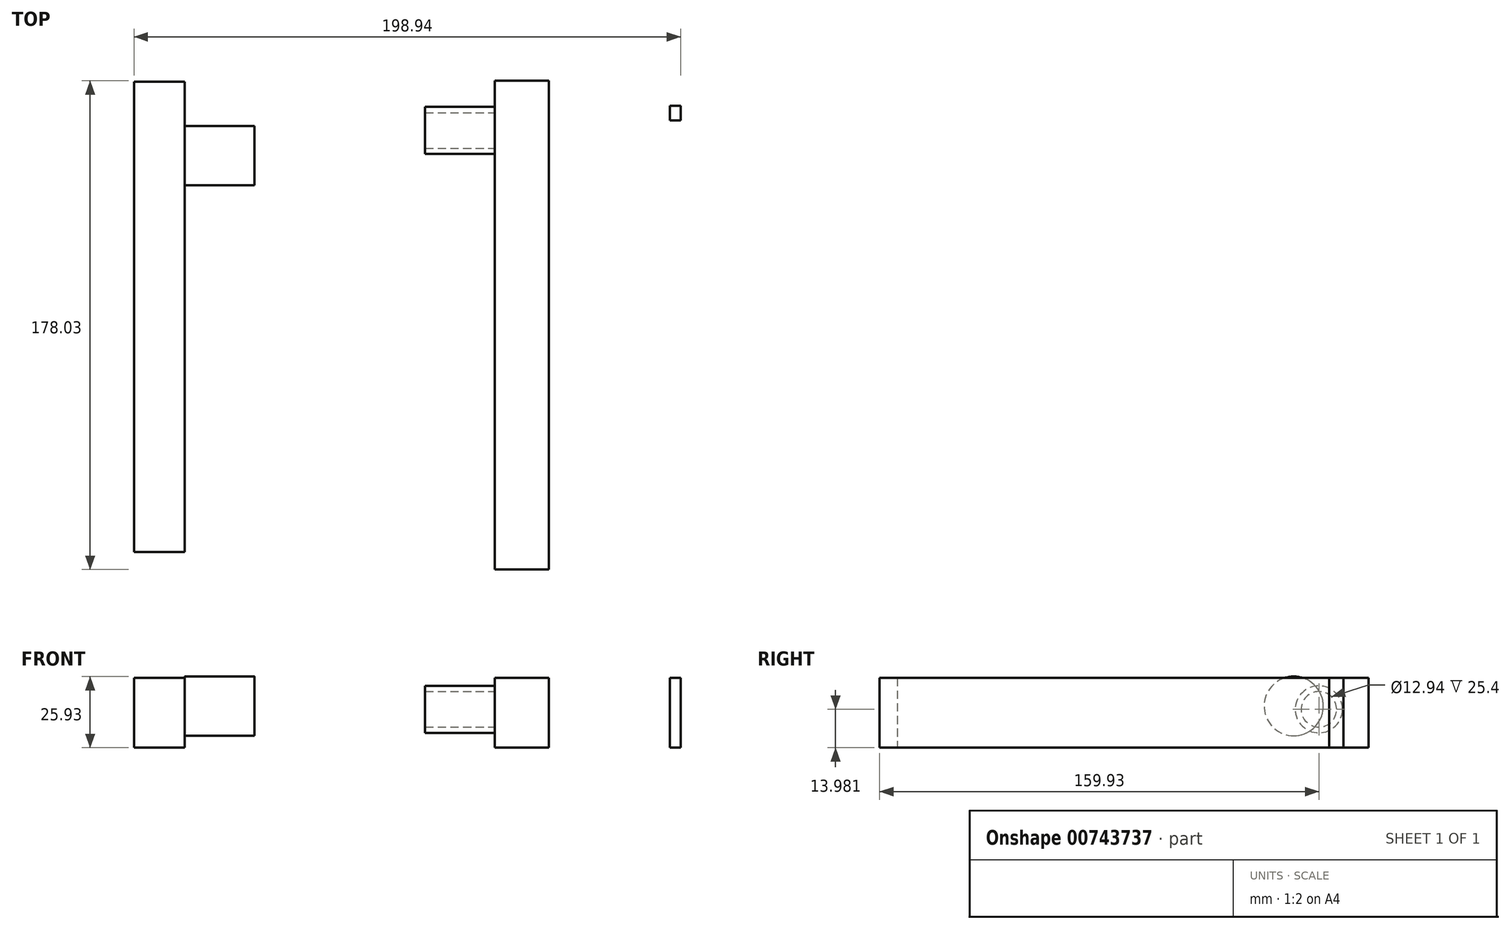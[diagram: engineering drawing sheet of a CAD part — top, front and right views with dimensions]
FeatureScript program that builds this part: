
annotation { "Feature Type Name" : "Feature", "Feature Type Description" : "" }
export const myFeature = defineFeature(function(context is Context, id is Id, definition is map)
    precondition{}
    {
        {
            var Q0;
            Q0=qCreatedBy(makeId("Top.planeOp"),FACE);
            var sketch = newSketch(context, id + "F0", { "sketchPlane" : qUnion([Q0])});
            skLineSegment(sketch, "E0.bottom", {"start": v(119.59, 61.49) * mm, "end": v(123.48, 61.49) * mm});
            skLineSegment(sketch, "E0.top", {"start": v(119.59, 66.74) * mm, "end": v(123.48, 66.74) * mm});
            skLineSegment(sketch, "E0.left", {"start": v(119.59, 61.49) * mm, "end": v(119.59, 66.74) * mm});
            skLineSegment(sketch, "E0.right", {"start": v(123.48, 61.49) * mm, "end": v(123.48, 66.74) * mm});
            skLineSegment(sketch, "E1.bottom", {"start": v(75.55, 75.89) * mm, "end": v(55.9, 75.89) * mm});
            skLineSegment(sketch, "E1.top", {"start": v(75.55, -102.14) * mm, "end": v(55.9, -102.14) * mm});
            skLineSegment(sketch, "E1.left", {"start": v(75.55, 75.89) * mm, "end": v(75.55, -102.14) * mm});
            skLineSegment(sketch, "E1.right", {"start": v(55.9, 75.89) * mm, "end": v(55.9, -102.14) * mm});
            skLineSegment(sketch, "E2.bottom", {"start": v(-75.46, 75.57) * mm, "end": v(-57, 75.57) * mm});
            skLineSegment(sketch, "E2.top", {"start": v(-75.46, -95.76) * mm, "end": v(-57, -95.76) * mm});
            skLineSegment(sketch, "E2.left", {"start": v(-75.46, 75.57) * mm, "end": v(-75.46, -95.76) * mm});
            skLineSegment(sketch, "E2.right", {"start": v(-57, 75.57) * mm, "end": v(-57, -95.76) * mm});
            skSolve(sketch);
        }
        {
            var Q0;
            Q0 = qSketchRegion(id + "F0", true);
            extrude(context, id + "F1", {"entities" : qUnion([Q0]), "depth" : 25.4 * mm, "offsetDistance" : 25.4 * mm});
        }
        {
            var Q0;
            Q0=makeQuery(id+"F1.opExtrude","SWEPT_FACE",FACE,{"disambiguationData":[OSD([sQuery(id+"F0.wireOp",EDGE,"E1.right")])]});
            var sketch = newSketch(context, id + "F2", { "sketchPlane" : qUnion([Q0])});
            skCircle(sketch, "E3", {"center": v(-57.79, 13.98) * mm, "radius": 6.47 * mm});
            skCircle(sketch, "E4", {"center": v(-57.79, 13.98) * mm, "radius": 8.57 * mm});
            skSolve(sketch);
        }
        {
            var Q0;
            Q0 = qSketchRegion(id + "F2", true);
            extrude(context, id + "F3", {"entities" : qUnion([Q0]), "operationType" : NewBodyOperationType.ADD, "depth" : 25.4 * mm, "offsetDistance" : 25.4 * mm});
        }
        {
            var Q0;
            Q0=makeQuery(id+"F1.opExtrude","SWEPT_FACE",FACE,{"disambiguationData":[OSD([sQuery(id+"F0.wireOp",EDGE,"E2.right")])]});
            var sketch = newSketch(context, id + "F4", { "sketchPlane" : qUnion([Q0])});
            skCircle(sketch, "E5", {"center": v(48.63, 15.15) * mm, "radius": 10.78 * mm});
            skPoint(sketch, "E5.first.point", {"position": v(59.08, 12.48) * mm});
            skPoint(sketch, "E5.second.point", {"position": v(38.28, 12.15) * mm});
            skPoint(sketch, "E5.third.point", {"position": v(51.96, 25.4) * mm});
            skSolve(sketch);
        }
        {
            var Q0;
            Q0 = qSketchRegion(id + "F4", true);
            extrude(context, id + "F5", {"entities" : qUnion([Q0]), "operationType" : NewBodyOperationType.ADD, "depth" : 25.4 * mm, "offsetDistance" : 25.4 * mm});
        }
    });
